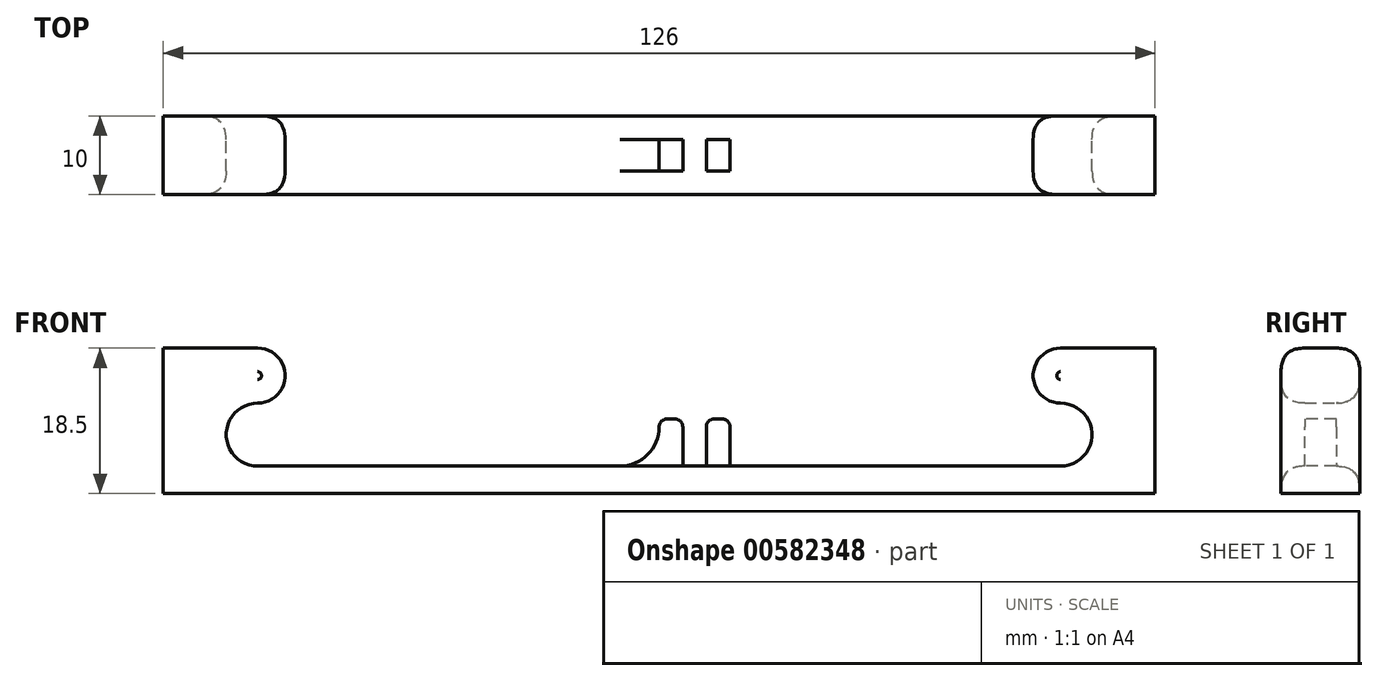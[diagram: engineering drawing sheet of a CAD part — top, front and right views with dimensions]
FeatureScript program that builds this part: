
annotation { "Feature Type Name" : "Feature", "Feature Type Description" : "" }
export const myFeature = defineFeature(function(context is Context, id is Id, definition is map)
    precondition{}
    {
        {
            var Q0;
            Q0=qCreatedBy(makeId("Front.planeOp"),FACE);
            var sketch = newSketch(context, id + "F0", { "sketchPlane" : qUnion([Q0])});
            skLineSegment(sketch, "E0", {"start": v(0, 18.5) * mm, "end": v(0, 0) * mm});
            skLineSegment(sketch, "E1", {"start": v(0, 0) * mm, "end": v(63, 0) * mm});
            skLineSegment(sketch, "E2", {"start": v(0, 18.5) * mm, "end": v(12, 18.5) * mm});
            skLineSegment(sketch, "E3", {"start": v(12, 3.5) * mm, "end": v(63, 3.5) * mm});
            skArc(sketch, "E4", {"start": v(12, 18.5) * mm, "mid": v(15.5, 15) * mm, "end": v(12, 11.5) * mm});
            skLineSegment(sketch, "E5", {"start": v(12, 18.5) * mm, "end": v(12, 0) * mm, "construction": true});
            skPoint(sketch, "E6", {"position": v(63, 0) * mm});
            skLineSegment(sketch, "E7", {"start": v(63, 44.38) * mm, "end": v(63, -37.8) * mm, "construction": true});
            skArc(sketch, "E8.MirrorCS", {"start": v(12, 11.5) * mm, "mid": v(8, 7.5) * mm, "end": v(12, 3.5) * mm});
            skPoint(sketch, "E9.MirrorCS.end.orphan", {"position": v(12, 3.5) * mm});
            skPoint(sketch, "E9.MirrorCS.start.orphan", {"position": v(12, 11.5) * mm});
            skLineSegment(sketch, "E10.MirrorCS", {"start": v(126, 0) * mm, "end": v(63, 0) * mm});
            skLineSegment(sketch, "E11.MirrorCS", {"start": v(114, 3.5) * mm, "end": v(63, 3.5) * mm});
            skArc(sketch, "E12.MirrorCS", {"start": v(114, 11.5) * mm, "mid": v(118, 7.5) * mm, "end": v(114, 3.5) * mm});
            skArc(sketch, "E13.MirrorCS", {"start": v(114, 18.5) * mm, "mid": v(110.5, 15) * mm, "end": v(114, 11.5) * mm});
            skLineSegment(sketch, "E14.MirrorCS", {"start": v(126, 18.5) * mm, "end": v(114, 18.5) * mm});
            skLineSegment(sketch, "E15.MirrorCS", {"start": v(126, 18.5) * mm, "end": v(126, 0) * mm});
            skLineSegment(sketch, "E16.MirrorCS", {"start": v(114, 18.5) * mm, "end": v(114, 0) * mm, "construction": true});
            skLineSegment(sketch, "E17", {"start": v(14, 28.4) * mm, "end": v(14, -16.13) * mm, "construction": true});
            skLineSegment(sketch, "E18", {"start": v(8, 7.5) * mm, "end": v(14, 7.5) * mm, "construction": true});
            skLineSegment(sketch, "E19.MirrorCS", {"start": v(118, 7.5) * mm, "end": v(112, 7.5) * mm, "construction": true});
            skSolve(sketch);
        }
        {
            var Q0;
            Q0 = qSketchRegion(id + "F0", true);
            extrude(context, id + "F1", {"entities" : qUnion([Q0]), "depth" : 10 * mm, "offsetDistance" : 25 * mm});
        }
        {
            var Q0;
            Q0=makeQuery(id+"F1.opExtrude","CAP_EDGE",EDGE,{"disambiguationData":[OSD([sQuery(id+"F0.wireOp",EDGE,"E13.MirrorCS")])],"isStart":true});
            var Q1;
            Q1=makeQuery(id+"F1.opExtrude","CAP_EDGE",EDGE,{"disambiguationData":[OSD([sQuery(id+"F0.wireOp",EDGE,"E13.MirrorCS")])],"isStart":false});
            var Q2;
            Q2=makeQuery(id+"F1.opExtrude","CAP_EDGE",EDGE,{"disambiguationData":[OSD([sQuery(id+"F0.wireOp",EDGE,"E4")])],"isStart":true});
            var Q3;
            Q3=makeQuery(id+"F1.opExtrude","CAP_EDGE",EDGE,{"disambiguationData":[OSD([sQuery(id+"F0.wireOp",EDGE,"E4")])],"isStart":false});
            fillet(context, id + "F2", {"entities" : qUnion([Q0, Q1, Q2, Q3]), "radius" : 3 * mm, "tangentPropagation" : true, "rho" : 0.5, "crossSection" : FilletCrossSection.CONIC, "allowEdgeOverflow" : false});
        }
        {
            var Q0;
            Q0=makeQuery(id+"F1.opExtrude","SWEPT_FACE",FACE,{"disambiguationData":[OSD([sQuery(id+"F0.wireOp",EDGE,"E3"),sQuery(id+"F0.wireOp",EDGE,"E11.MirrorCS")])]});
            var sketch = newSketch(context, id + "F3", { "sketchPlane" : qUnion([Q0])});
            skLineSegment(sketch, "E20.bottom", {"start": v(63, -10) * mm, "end": v(66, -10) * mm});
            skLineSegment(sketch, "E20.top", {"start": v(63, 0) * mm, "end": v(66, 0) * mm});
            skLineSegment(sketch, "E20.left", {"start": v(63, 0) * mm, "end": v(63, -10) * mm});
            skLineSegment(sketch, "E20.right", {"start": v(66, 0) * mm, "end": v(66, -10) * mm});
            skLineSegment(sketch, "E21.bottom", {"start": v(69, -10) * mm, "end": v(72, -10) * mm});
            skLineSegment(sketch, "E21.top", {"start": v(69, 0) * mm, "end": v(72, 0) * mm});
            skLineSegment(sketch, "E21.left", {"start": v(69, 0) * mm, "end": v(69, -10) * mm});
            skLineSegment(sketch, "E21.right", {"start": v(72, 0) * mm, "end": v(72, -10) * mm});
            skLineSegment(sketch, "E22", {"start": v(1.11, -5) * mm, "end": v(126, -5) * mm, "construction": true});
            skPoint(sketch, "E22.startSnap0", {"position": v(0, -5) * mm});
            skSolve(sketch);
        }
        {
            var Q0;
            Q0=makeQuery(id+"F3.imprint","IMPRINT",FACE,{"disambiguationData":[TD([[makeQuery(id+"F3.imprint","IMPRINT",EDGE,{"derivedFrom":sQuery(id+"F3.wireOp",EDGE,"E20.bottom")}),-1.0]])]});
            var Q1;
            Q1=makeQuery(id+"F3.imprint","IMPRINT",FACE,{"disambiguationData":[TD([[makeQuery(id+"F3.imprint","IMPRINT",EDGE,{"derivedFrom":sQuery(id+"F3.wireOp",EDGE,"E21.bottom")}),-1.0]])]});
            var Q2;
            {var subQ0=sQuery(id+"F3.wireOp",EDGE,"E21.left");var subQ1=sQuery(id+"F0.wireOp",EDGE,"E11.MirrorCS");var subQ2=sQuery(id+"F0.wireOp",EDGE,"E3");var subQ3=makeQuery(id+"F1.opExtrude","SWEPT_FACE",FACE,{"disambiguationData":[OSD([subQ2,subQ1])]});var subQ4=makeQuery(id+"F2.opFillet","BLEND_EDGE",EDGE,{"blendedFrom":[makeQuery(id+"F1.opExtrude","CAP_EDGE",EDGE,{"disambiguationData":[OSD([subQ2,subQ1])],"isStart":true}),subQ3],"blendedInto":[subQ3]});var subQ5=makeQuery(id+"F3.imprint","INTERSECT",VERTEX,{"derivedFrom":[subQ4,subQ0]});Q2=makeQuery(id+"F3.imprint","IMPRINT",FACE,{"disambiguationData":[TD([[makeQuery(id+"F3.imprint","IMPRINT",EDGE,{"disambiguationData":[TD([[subQ5,-1.0]])],"derivedFrom":subQ0}),1.0]])]});}
            var Q3;
            {var subQ0=sQuery(id+"F3.wireOp",EDGE,"E20.left");var subQ1=sQuery(id+"F0.wireOp",EDGE,"E11.MirrorCS");var subQ2=sQuery(id+"F0.wireOp",EDGE,"E3");var subQ3=makeQuery(id+"F1.opExtrude","SWEPT_FACE",FACE,{"disambiguationData":[OSD([subQ2,subQ1])]});var subQ4=makeQuery(id+"F2.opFillet","BLEND_EDGE",EDGE,{"blendedFrom":[makeQuery(id+"F1.opExtrude","CAP_EDGE",EDGE,{"disambiguationData":[OSD([subQ2,subQ1])],"isStart":true}),subQ3],"blendedInto":[subQ3]});var subQ5=makeQuery(id+"F3.imprint","INTERSECT",VERTEX,{"derivedFrom":[subQ4,subQ0]});Q3=makeQuery(id+"F3.imprint","IMPRINT",FACE,{"disambiguationData":[TD([[makeQuery(id+"F3.imprint","IMPRINT",EDGE,{"disambiguationData":[TD([[subQ5,-1.0]])],"derivedFrom":subQ0}),1.0]])]});}
            extrude(context, id + "F4", {"entities" : qUnion([Q0, Q1, Q2, Q3]), "operationType" : NewBodyOperationType.ADD, "depth" : 6 * mm, "offsetDistance" : 25 * mm});
        }
        {
            var Q0;
            Q0=makeQuery(id+"F4.opExtrude","CAP_EDGE",EDGE,{"disambiguationData":[OSD([sQuery(id+"F3.wireOp",EDGE,"E20.left")])],"isStart":false});
            var Q1;
            Q1=makeQuery(id+"F4.opExtrude","CAP_EDGE",EDGE,{"disambiguationData":[OSD([sQuery(id+"F3.wireOp",EDGE,"E21.right")])],"isStart":false});
            var Q2;
            Q2=makeQuery(id+"F4.opExtrude","CAP_EDGE",EDGE,{"disambiguationData":[OSD([sQuery(id+"F3.wireOp",EDGE,"E21.left")])],"isStart":false});
            var Q3;
            Q3=makeQuery(id+"F4.opExtrude","CAP_EDGE",EDGE,{"disambiguationData":[OSD([sQuery(id+"F3.wireOp",EDGE,"E20.right")])],"isStart":false});
            fillet(context, id + "F5", {"entities" : qUnion([Q0, Q1, Q2, Q3]), "radius" : 1 * mm, "tangentPropagation" : true, "allowEdgeOverflow" : false});
        }
        {
            var Q0;
            Q0=makeQuery(id+"F4.opExtrude","CAP_EDGE",EDGE,{"disambiguationData":[OSD([sQuery(id+"F3.wireOp",EDGE,"E20.left")])],"isStart":true});
            var Q1;
            Q1=makeQuery(id+"F4.opExtrude","CAP_EDGE",EDGE,{"disambiguationData":[OSD([sQuery(id+"F3.wireOp",EDGE,"E21.right")])],"isStart":true});
            fillet(context, id + "F6", {"entities" : qUnion([Q0, Q1]), "radius" : 5 * mm, "tangentPropagation" : true, "allowEdgeOverflow" : false});
        }
    });
